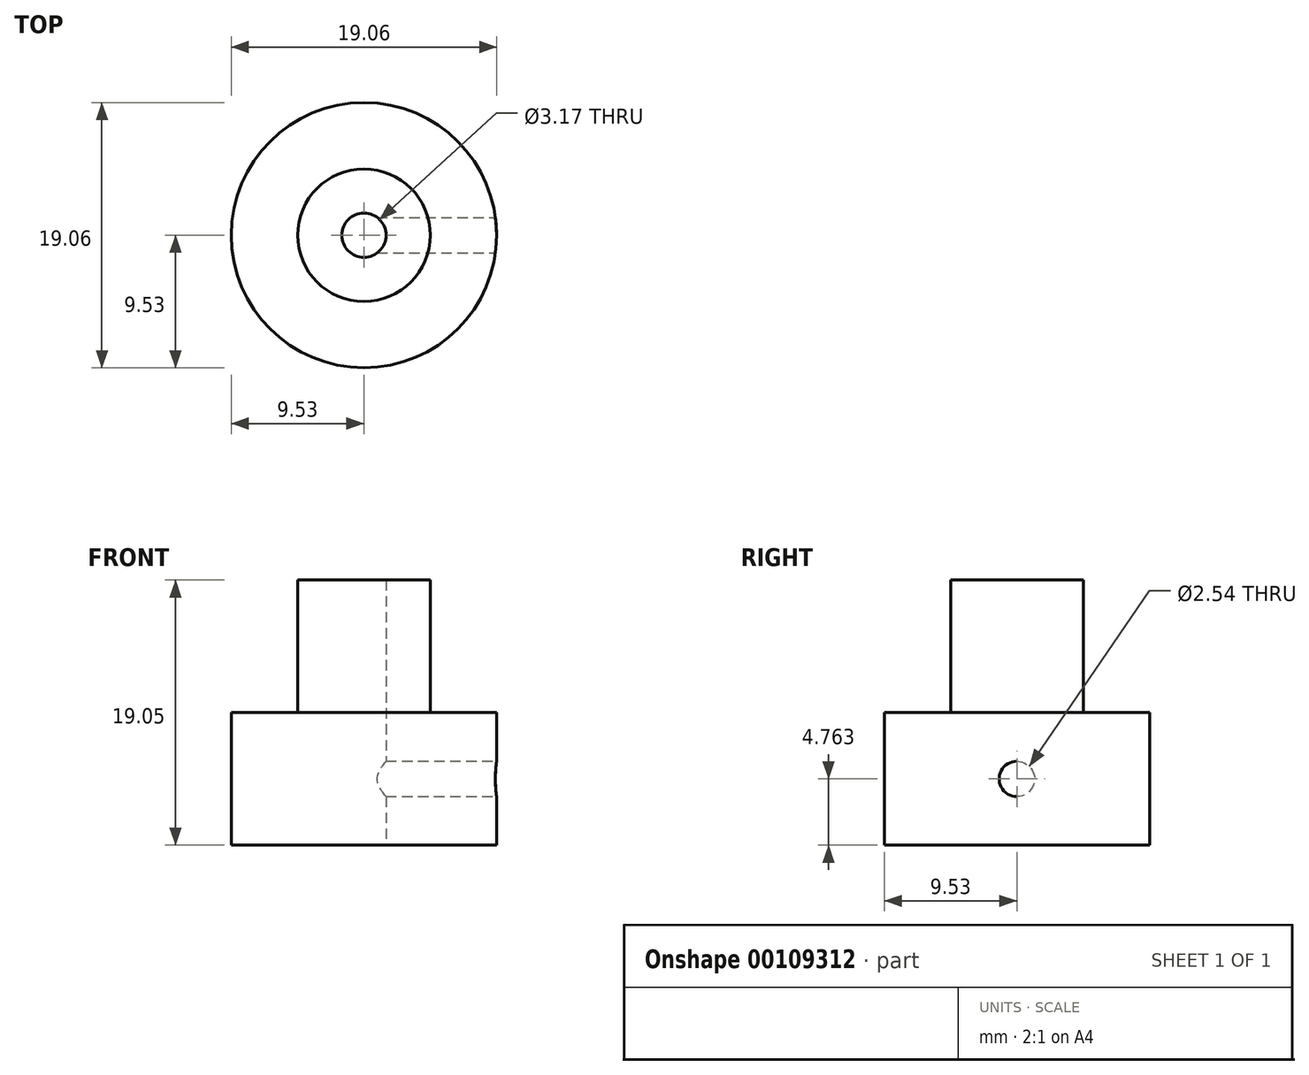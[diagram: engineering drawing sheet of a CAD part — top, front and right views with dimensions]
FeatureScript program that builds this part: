
annotation { "Feature Type Name" : "Feature", "Feature Type Description" : "" }
export const myFeature = defineFeature(function(context is Context, id is Id, definition is map)
    precondition{}
    {
        {
            var Q0;
            Q0=qCreatedBy(makeId("Top.planeOp"),FACE);
            var sketch = newSketch(context, id + "F0", { "sketchPlane" : qUnion([Q0])});
            skCircle(sketch, "E0", {"center": v(0, 0) * mm, "radius": 9.53 * mm});
            skCircle(sketch, "E1", {"center": v(0, 0) * mm, "radius": 1.59 * mm});
            skSolve(sketch);
        }
        {
            var Q0;
            Q0=makeQuery(id+"F0.imprint","IMPRINT",FACE,{"disambiguationData":[TD([[makeQuery(id+"F0.imprint","IMPRINT",EDGE,{"derivedFrom":sQuery(id+"F0.wireOp",EDGE,"E0")}),1.0]])]});
            extrude(context, id + "F1", {"entities" : qUnion([Q0]), "depth" : 9.52 * mm});
        }
        {
            var Q0;
            Q0=makeQuery(id+"F1.opExtrude","CAP_FACE",FACE,{"disambiguationData":[OSD([sQuery(id+"F0.wireOp",EDGE,"E0"),sQuery(id+"F0.wireOp",EDGE,"E1")])],"isStart":false});
            var sketch = newSketch(context, id + "F2", { "sketchPlane" : qUnion([Q0])});
            skCircle(sketch, "E2", {"center": v(0, 0) * mm, "radius": 4.76 * mm});
            skCircle(sketch, "E3.0", {"center": v(0, 0) * mm, "radius": 1.59 * mm});
            skSolve(sketch);
        }
        {
            var Q0;
            Q0 = qSketchRegion(id + "F2", true);
            extrude(context, id + "F3", {"entities" : qUnion([Q0]), "operationType" : NewBodyOperationType.ADD, "depth" : 9.52 * mm});
        }
        {
            var Q0;
            Q0=qCreatedBy(makeId("Right.planeOp"),FACE);
            cPlane(context, id + "F4", {"entities" : qUnion([Q0]), "cplaneType" : CPlaneType.OFFSET, "offset" : 9.52 * mm, "width" : 152.4 * mm, "height" : 152.4 * mm});
        }
        {
            var Q0;
            Q0=qCreatedBy(id+"F4.planeOp",FACE);
            var sketch = newSketch(context, id + "F5", { "sketchPlane" : qUnion([Q0])});
            skLineSegment(sketch, "E4.0", {"start": v(-9.53, 9.53) * mm, "end": v(9.53, 9.53) * mm, "construction": true});
            skLineSegment(sketch, "E5.0", {"start": v(-9.53, 0) * mm, "end": v(9.53, 0) * mm, "construction": true});
            skLineSegment(sketch, "E6", {"start": v(0, 9.53) * mm, "end": v(0, 0) * mm, "construction": true});
            skCircle(sketch, "E7", {"center": v(0, 4.76) * mm, "radius": 1.27 * mm});
            skSolve(sketch);
        }
        {
            var Q0;
            Q0 = qSketchRegion(id + "F5", true);
            extrude(context, id + "F6", {"entities" : qUnion([Q0]), "operationType" : NewBodyOperationType.REMOVE, "oppositeDirection" : true, "depth" : 9.52 * mm});
        }
    });
